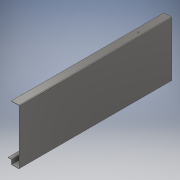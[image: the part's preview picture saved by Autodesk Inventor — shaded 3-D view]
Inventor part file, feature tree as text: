
AUTODESK INVENTOR PART (.ipt)
format: ipt  version: 2017 (Build 210142000, 142)  size: 253,440 bytes
history: native  units: in
note: dims shown in document units (in); Inventor stores cm internally (conversion verified against a paired STEP export)
features: other x6, sketch x3, plane x1
ambient origin geometry x8: Origin, YZ Plane, XZ Plane, XY Plane, X Axis, Y Axis, Z Axis, Center Point
bodies: Solid1 (feature_tree)
feature tree (10):
  other  "Lateral -A.ipt"
  plane  "Work Plane1"
  other  "Decal1"
  other  "Solid1::Lateral -A.ipt"
  other  "TaggingFeature1"
  sketch  "Sketch1"  dims[d0=0.3937in]
  sketch  "Sketch2"  dims[d1=7.874in]
  sketch  "Sketch3"
  other  "Image1"
  other  "Definition1"
